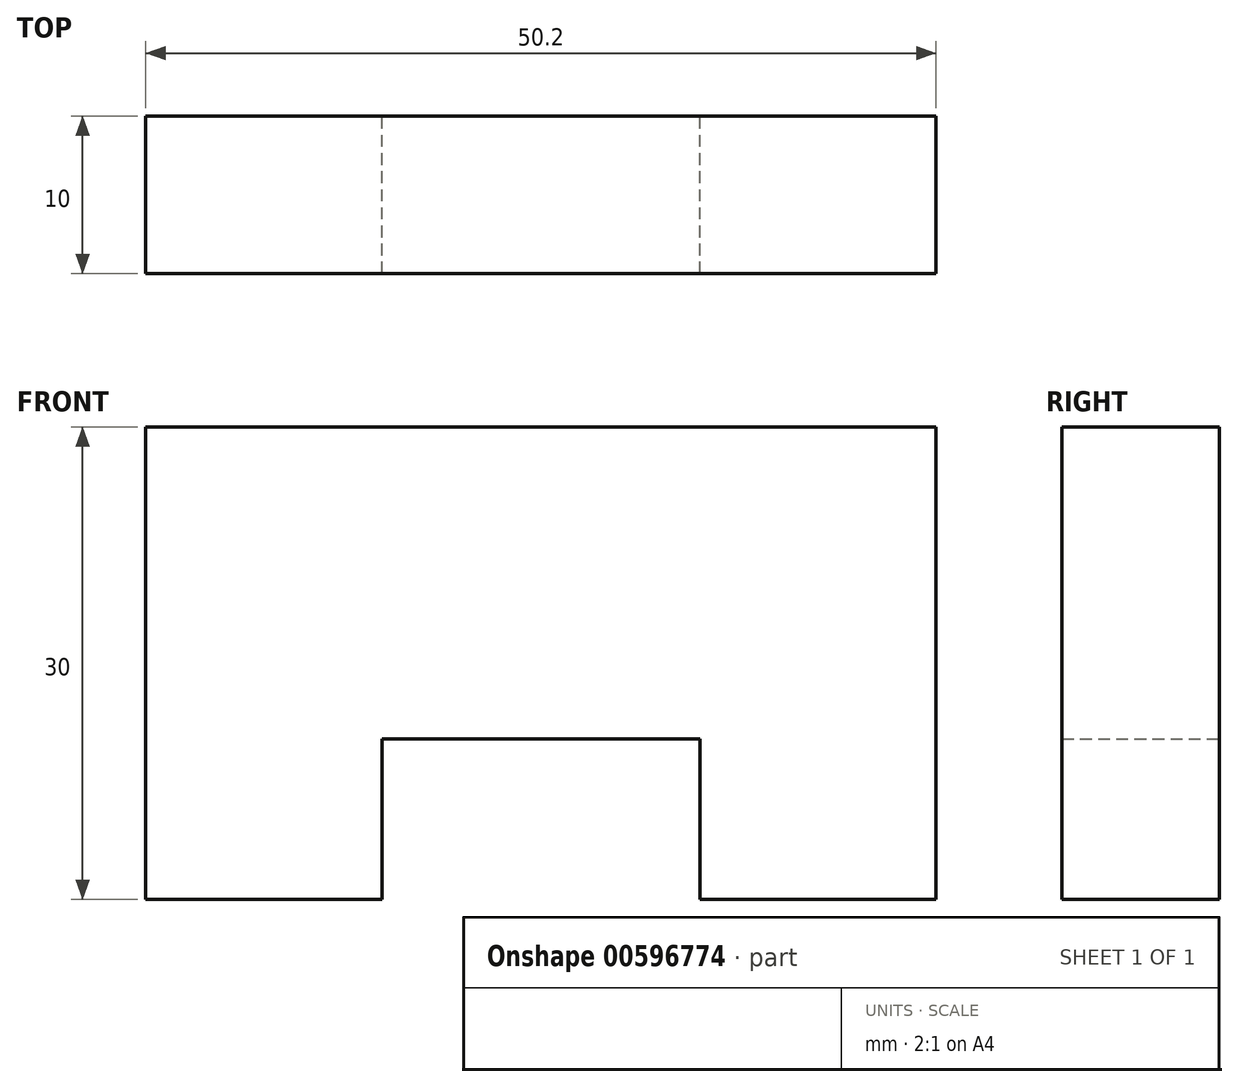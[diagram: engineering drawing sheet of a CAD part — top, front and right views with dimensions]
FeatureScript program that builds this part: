
annotation { "Feature Type Name" : "Feature", "Feature Type Description" : "" }
export const myFeature = defineFeature(function(context is Context, id is Id, definition is map)
    precondition{}
    {
        {
            var Q0;
            Q0=qCreatedBy(makeId("Front.planeOp"),FACE);
            var sketch = newSketch(context, id + "F0", { "sketchPlane" : qUnion([Q0])});
            skLineSegment(sketch, "E0", {"start": v(-10.1, 0) * mm, "end": v(-25.1, 0) * mm});
            skLineSegment(sketch, "E1", {"start": v(-25.1, 0) * mm, "end": v(-25.1, 30) * mm});
            skLineSegment(sketch, "E2", {"start": v(-25.1, 30) * mm, "end": v(25.1, 30) * mm});
            skLineSegment(sketch, "E3", {"start": v(25.1, 30) * mm, "end": v(25.1, 0) * mm});
            skLineSegment(sketch, "E4", {"start": v(25.1, 0) * mm, "end": v(10.1, 0) * mm});
            skLineSegment(sketch, "E5", {"start": v(10.1, 0) * mm, "end": v(10.1, 10.2) * mm});
            skLineSegment(sketch, "E6", {"start": v(10.1, 10.2) * mm, "end": v(-10.1, 10.2) * mm});
            skLineSegment(sketch, "E7", {"start": v(-10.1, 10.2) * mm, "end": v(-10.1, 0) * mm});
            skSolve(sketch);
        }
        {
            var Q0;
            Q0=makeQuery(id+"F0.imprint","IMPRINT",FACE,{"disambiguationData":[TD([[makeQuery(id+"F0.imprint","IMPRINT",EDGE,{"derivedFrom":sQuery(id+"F0.wireOp",EDGE,"E0")}),-1.0]])]});
            extrude(context, id + "F1", {"entities" : qUnion([Q0]), "depth" : 10 * mm, "offsetDistance" : 25 * mm});
        }
    });
